# Revit family: AMY1_63_UN_Inlay LED_ETK
name_source: partatom
category: Lighting Fixtures
revit_build: Autodesk Revit 2017 (Build: 20190508_0315(x64)
units: mm (PartAtom-declared; Revit-internal decimal feet)

## family parameters
Always vertical = Yes
Cut with Voids When Loaded = No
Light Source = No
OmniClass Number = 23.80.70.11.14.11
OmniClass Title = Downlights
Part Type = Normal
Room Calculation Point = Yes
Round Connector Dimension = Use Diameter
Shared = No
Work Plane-Based = No

## types (8) — shared parameters
Assembly Code = 63.0
Bundle = 85°/89°
Description = Recessed/inlay LED
IfcExportAs = IfcLightFixtureType
IfcExportType = USERDEFINED
Lamp = LED
Luminaire_Body_Material = PPS Plastic
Manufacturer = ETK B.V.
Model = AMY.1
URL = https://www.etk.nl
Voltage = 230 V

## per-type parameters (varying)
| type | Apparent Load | Light Source | Wattage Comments |
| AMY.1100.15 - 22W / 3000lm / 3000K | 22 VA | AMY.1 - Lightsource : AMY.1100.15 - 22W / 3000lm / 3000K | 22W |
| AMY.1200.15 - 22W / 3100lm / 4000K | 22 VA | AMY.1 - Lightsource : AMY.1200.15 - 22W / 3100lm / 4000K | 22W |
| AMY.1300.15 - 31W / 4100lm / 3000K | 31 VA | AMY.1 - Lightsource : AMY.1300.15 - 31W / 4100lm / 3000K | 31W |
| AMY.1400.15 - 31W / 4250lm / 4000K | 31 VA | AMY.1 - Lightsource : AMY.1400.15 - 31W / 4250lm / 4000K | 31W |
| AMY.1103.15 - 22W / 3000lm / 3000K | 22 VA | AMY.1 - Lightsource : AMY.1103.15 - 22W / 3000lm / 3000K | 22W |
| AMY.1203.15 - 22W / 3100lm / 4000K | 22 VA | AMY.1 - Lightsource : AMY.1203.15 - 22W / 3100lm / 4000K | 22W |
| AMY.1303.15 - 31W / 4100lm / 3000K | 31 VA | AMY.1 - Lightsource : AMY.1303.15 - 31W / 4100lm / 3000K | 31W |
| AMY.1403.15 - 31W / 4250lm / 4000K | 31 VA | AMY.1 - Lightsource : AMY.1403.15 - 31W / 4250lm / 4000K | 31W |

## geometry (parser evidence)
native form markers: Sweep x5
no freeform markers — native parametric forms only
